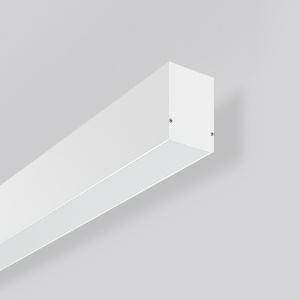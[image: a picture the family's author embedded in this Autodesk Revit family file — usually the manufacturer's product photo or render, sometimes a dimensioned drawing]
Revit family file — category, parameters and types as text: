
# Revit family: less_is_more_50_312608_002_1_ff8b
name_source: partatom
category: Lighting Fixtures
units: mm (PartAtom-declared; Revit-internal decimal feet)

## family parameters
Cut with Voids When Loaded = No
Host = Face
Light Source = No
Part Type = Normal
Room Calculation Point = No
Round Connector Dimension = Use Diameter
Shared = No

## types (1)
- LESS IS MORE 50 (1 x LED Modul 840, 2750 lm, 4000)
    Apparent Load = 20 VA
    CIE Flux Codes = 48 80 96 50 100
    Color Rendering = 80
    Color Temperature = 4000
    Default Elevation = 1800 mm
    Description = Series: LESS IS MORE 50
Linear wall luminaires. Housing: extruded aluminium profile, powder-coated. End cap aluminium powder-coated. Diffuser made of non-yellowing plastic (PMMA), opal. Direct 50%, indirect 50% light emission. Suitable for Wall (surface). LED unit with integrated converter interchangeable and removable. Suitable for through-wiring. With sensors or as a safety luminaire on request. 
Colour: traffic white, matt (RAL 9016)
Length: 1127 mm
Width: 67 mm
Height: 75 mm
Lamp: LED
Socket: without socket
Colour temperature: 4000K
Colour rendering index (CRI): 80
Light source: LED
Socket lamp2: Without base
Colour temperature: 4000K
Colour rendering index (CRI) 2: 80
System power: 20 W
Rated luminous flux: 2750 lm
Luminous efficiency: 138 lm/W
Control gear: Regulated power supply
Control gear: Regulated power supply
Protection class: I
Type of protection: IP 20
    Height = 75 mm
    Lamp = 1 x LED Modul 840
    Lamp Light Flux = 2750 lm
    Lamp count = 1
    Length = 1127 mm
    Lifetime = 50000 h
    Luminous efficacy = 138 lm/W
    Manufacturer = RZB
    ModVariant = No
    Model = 312608.002.1
    Mounting Place = Wall
    Mounting Type = Surface mounted
    Number of Poles = 1
    OnlyDefault = Yes
    Power Factor = 1
    Product Name = LESS IS MORE 50
    Product group = Surface mounted LED linear luminaires
    ProductGroupID = 2007
    Protection Class = Protection class I
    Protection Degree = IP 20
    RLX_Detail_Level = 1
    RLX_Emergency_Light_Flux = 0 lm
    RLX_Emergency_Type = 0
    RLX_Emergency_Type_DB = No
    RlxData = <blob elided: 39601 chars, md5=32d79727>
    Socket = socket
    Standby Power = 0 W
    System Light Flux = 2750 lm
    System Power = 20 W
    Type Comments = Product without accessories
    Type Image = 312606.002.jpg
    URL = http://relux.com
    VarID = ---
    Voltage = 0 V
    Weight = 0.00 kg
    Width = 67 mm

## geometry (parser evidence)
native form markers: Blend x4, Sweep x12
no freeform markers — native parametric forms only
